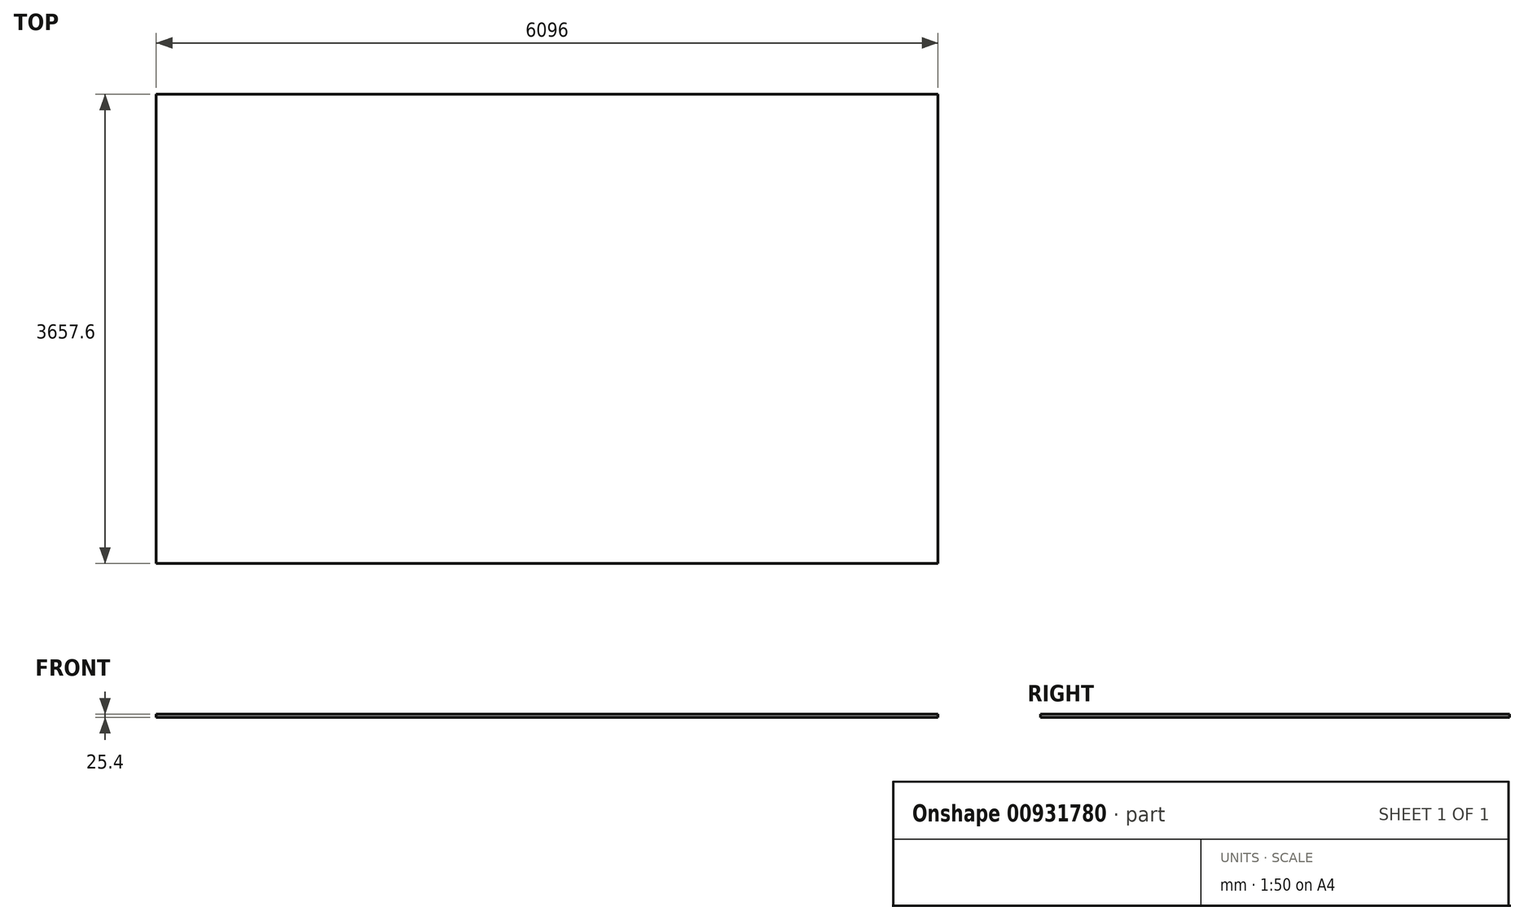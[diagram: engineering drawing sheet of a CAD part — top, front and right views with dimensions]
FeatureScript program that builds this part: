
annotation { "Feature Type Name" : "Feature", "Feature Type Description" : "" }
export const myFeature = defineFeature(function(context is Context, id is Id, definition is map)
    precondition{}
    {
        {
            var Q0;
            Q0=qCreatedBy(makeId("Top.planeOp"),FACE);
            var sketch = newSketch(context, id + "F0", { "sketchPlane" : qUnion([Q0])});
            skLineSegment(sketch, "E0.bottom", {"start": v(3048, 1828.8) * mm, "end": v(-3048, 1828.8) * mm});
            skLineSegment(sketch, "E0.top", {"start": v(3048, -1828.8) * mm, "end": v(-3048, -1828.8) * mm});
            skLineSegment(sketch, "E0.left", {"start": v(3048, 1828.8) * mm, "end": v(3048, -1828.8) * mm});
            skLineSegment(sketch, "E0.right", {"start": v(-3048, 1828.8) * mm, "end": v(-3048, -1828.8) * mm});
            skPoint(sketch, "E0.middle", {"position": v(0, 0) * mm});
            skSolve(sketch);
        }
        {
            var Q0;
            Q0 = qSketchRegion(id + "F0", true);
            extrude(context, id + "F1", {"entities" : qUnion([Q0]), "depth" : 25.4 * mm, "offsetDistance" : 25.4 * mm});
        }
    });
